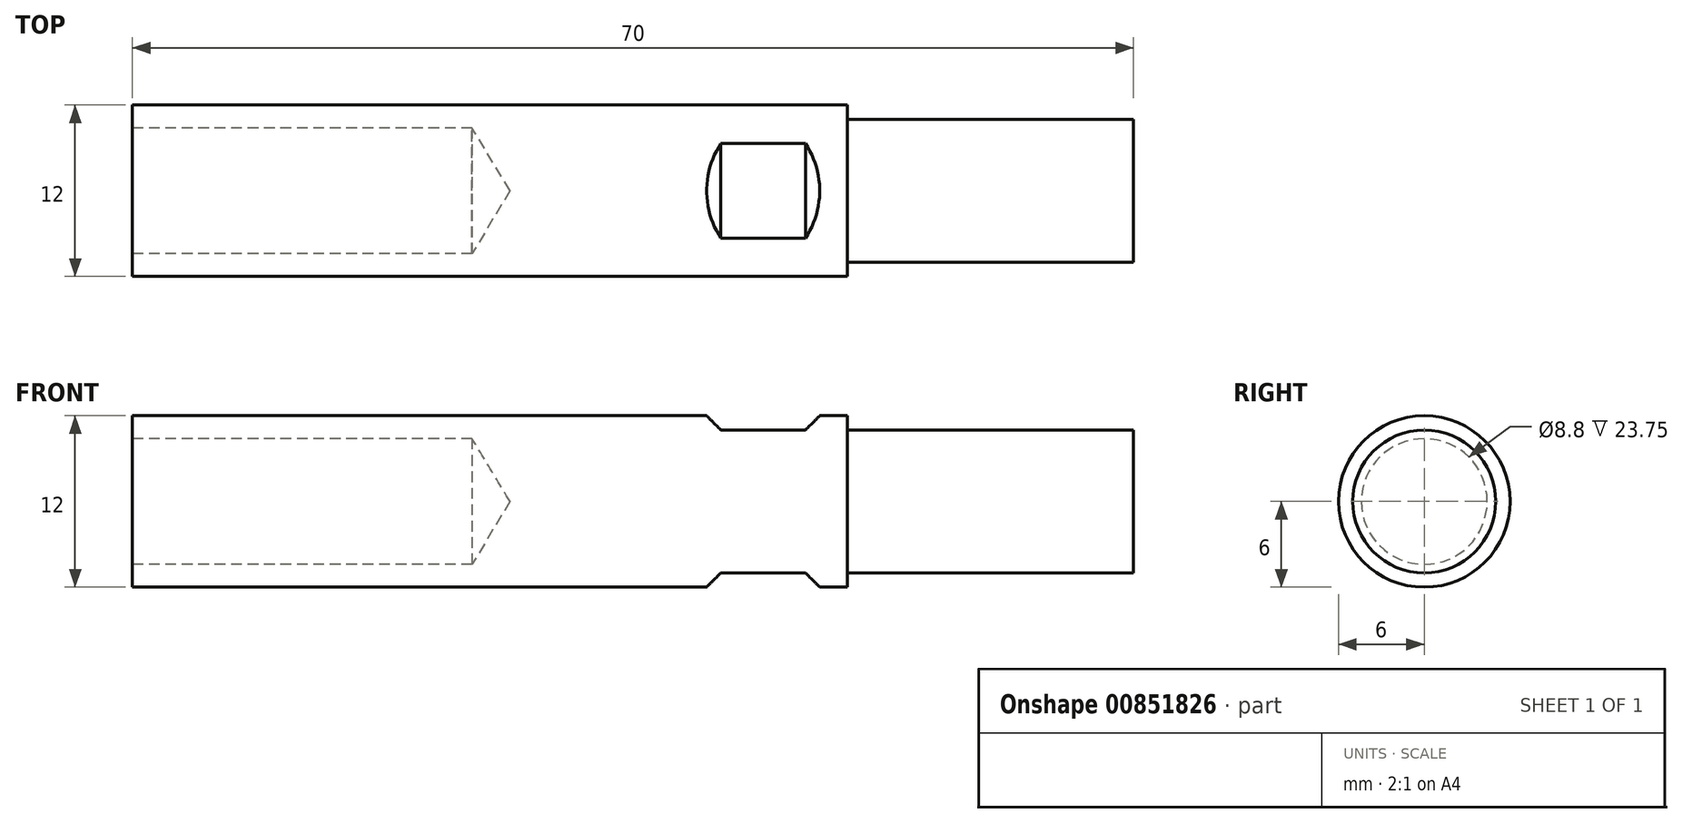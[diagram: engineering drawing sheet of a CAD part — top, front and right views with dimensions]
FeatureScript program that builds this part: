
annotation { "Feature Type Name" : "Feature", "Feature Type Description" : "" }
export const myFeature = defineFeature(function(context is Context, id is Id, definition is map)
    precondition{}
    {
        {
            var Q0;
            Q0=qCreatedBy(makeId("Right.planeOp"),FACE);
            var sketch = newSketch(context, id + "F0", { "sketchPlane" : qUnion([Q0])});
            skCircle(sketch, "E0", {"center": v(0, 0) * mm, "radius": 6 * mm});
            skSolve(sketch);
        }
        {
            var Q0;
            Q0=makeQuery(id+"F0.imprint","IMPRINT",FACE,{"disambiguationData":[TD([[makeQuery(id+"F0.imprint","IMPRINT",EDGE,{"derivedFrom":sQuery(id+"F0.wireOp",EDGE,"E0")}),1.0]])]});
            extrude(context, id + "F1", {"entities" : qUnion([Q0]), "depth" : 50 * mm, "offsetDistance" : 25 * mm});
        }
        {
            var Q0;
            Q0=makeQuery(id+"F1.opExtrude","CAP_FACE",FACE,{"disambiguationData":[OSD([sQuery(id+"F0.wireOp",EDGE,"E0")])],"isStart":false});
            var sketch = newSketch(context, id + "F2", { "sketchPlane" : qUnion([Q0])});
            skCircle(sketch, "E1", {"center": v(0, 0) * mm, "radius": 5 * mm});
            skSolve(sketch);
        }
        {
            var Q0;
            Q0=makeQuery(id+"F2.imprint","IMPRINT",FACE,{"disambiguationData":[TD([[makeQuery(id+"F2.imprint","IMPRINT",EDGE,{"derivedFrom":sQuery(id+"F2.wireOp",EDGE,"E1")}),1.0]])]});
            extrude(context, id + "F3", {"entities" : qUnion([Q0]), "operationType" : NewBodyOperationType.ADD, "depth" : 20 * mm, "offsetDistance" : 25 * mm});
        }
        {
            var Q0;
            Q0=makeQuery(id+"F1.opExtrude","CAP_FACE",FACE,{"disambiguationData":[OSD([sQuery(id+"F0.wireOp",EDGE,"E0")])],"isStart":true});
            var sketch = newSketch(context, id + "F4", { "sketchPlane" : qUnion([Q0])});
            skPoint(sketch, "E2", {"position": v(0, 0) * mm});
            skSolve(sketch);
        }
        {
            var Q0;
            Q0=sQuery(id+"F4.wireOp",VERTEX,"E2");
            var Q1;
            Q1=makeQuery(id+"F1.opExtrude","SWEPT_BODY",BODY,{"disambiguationData":[OSD([sQuery(id+"F0.wireOp",EDGE,"E0")])]});
            hole(context, id + "F5", {"style" : HoleStyle.SIMPLE, "endStyle" : HoleEndStyle.BLIND, "standardTappedOrClearance" : lookupTablePath({ "standard" : "ISO", "engagement" : "75%", "pitch" : "1.25 mm", "size" : "M10", "type" : "Tapped" }), "standardBlindInLast" : lookupTablePath({ "standard" : "ISO", "engagement" : "75%", "pitch" : "1.25 mm", "size" : "M10", "type" : "Tapped" }), "holeDiameter" : 8.8 * mm, "majorDiameter" : 10 * mm, "showTappedDepth" : true, "holeDepth" : 23.75 * mm, "isTappedThrough" : true, "tappedDepth" : 20 * mm, "tapClearance" : 3, "locations" : qUnion([Q0]), "scope" : qUnion([Q1])});
        }
        {
            var Q0;
            Q0=qCreatedBy(makeId("Front.planeOp"),FACE);
            var sketch = newSketch(context, id + "F6", { "sketchPlane" : qUnion([Q0])});
            skLineSegment(sketch, "E3.bottom", {"start": v(40.1, 13) * mm, "end": v(48.1, 13) * mm});
            skLineSegment(sketch, "E3.top", {"start": v(41.15, 5) * mm, "end": v(47.06, 5) * mm});
            skLineSegment(sketch, "E3.left", {"start": v(40.1, 13) * mm, "end": v(40.1, 6.04) * mm});
            skLineSegment(sketch, "E3.right", {"start": v(48.1, 13) * mm, "end": v(48.1, 6.04) * mm});
            skLineSegment(sketch, "E4", {"start": v(40.1, 6.04) * mm, "end": v(41.15, 5) * mm});
            skLineSegment(sketch, "E5", {"start": v(47.06, 5) * mm, "end": v(48.1, 6.04) * mm});
            skPoint(sketch, "E6.orphan", {"position": v(48.1, 5) * mm});
            skLineSegment(sketch, "E7.MirrorCS", {"start": v(41.15, -5) * mm, "end": v(47.06, -5) * mm});
            skLineSegment(sketch, "E8.MirrorCS", {"start": v(47.06, -5) * mm, "end": v(48.1, -6.04) * mm});
            skLineSegment(sketch, "E9.MirrorCS", {"start": v(48.1, -13) * mm, "end": v(48.1, -6.04) * mm});
            skLineSegment(sketch, "E10.MirrorCS", {"start": v(40.1, -13) * mm, "end": v(48.1, -13) * mm});
            skLineSegment(sketch, "E11.MirrorCS", {"start": v(40.1, -13) * mm, "end": v(40.1, -6.04) * mm});
            skLineSegment(sketch, "E12.MirrorCS", {"start": v(40.1, -6.04) * mm, "end": v(41.15, -5) * mm});
            skSolve(sketch);
        }
        {
            var Q0;
            Q0=makeQuery(id+"F6.imprint","IMPRINT",FACE,{"disambiguationData":[TD([[makeQuery(id+"F6.imprint","IMPRINT",EDGE,{"derivedFrom":sQuery(id+"F6.wireOp",EDGE,"E3.bottom")}),-1.0]])]});
            var Q1;
            Q1=makeQuery(id+"F6.imprint","IMPRINT",FACE,{"disambiguationData":[TD([[makeQuery(id+"F6.imprint","IMPRINT",EDGE,{"derivedFrom":sQuery(id+"F6.wireOp",EDGE,"E7.MirrorCS")}),-1.0]])]});
            extrude(context, id + "F7", {"entities" : qUnion([Q0, Q1]), "operationType" : NewBodyOperationType.REMOVE, "endBound" : BoundingType.SYMMETRIC, "oppositeDirection" : true, "depth" : 25 * mm, "offsetDistance" : 25 * mm});
        }
    });
